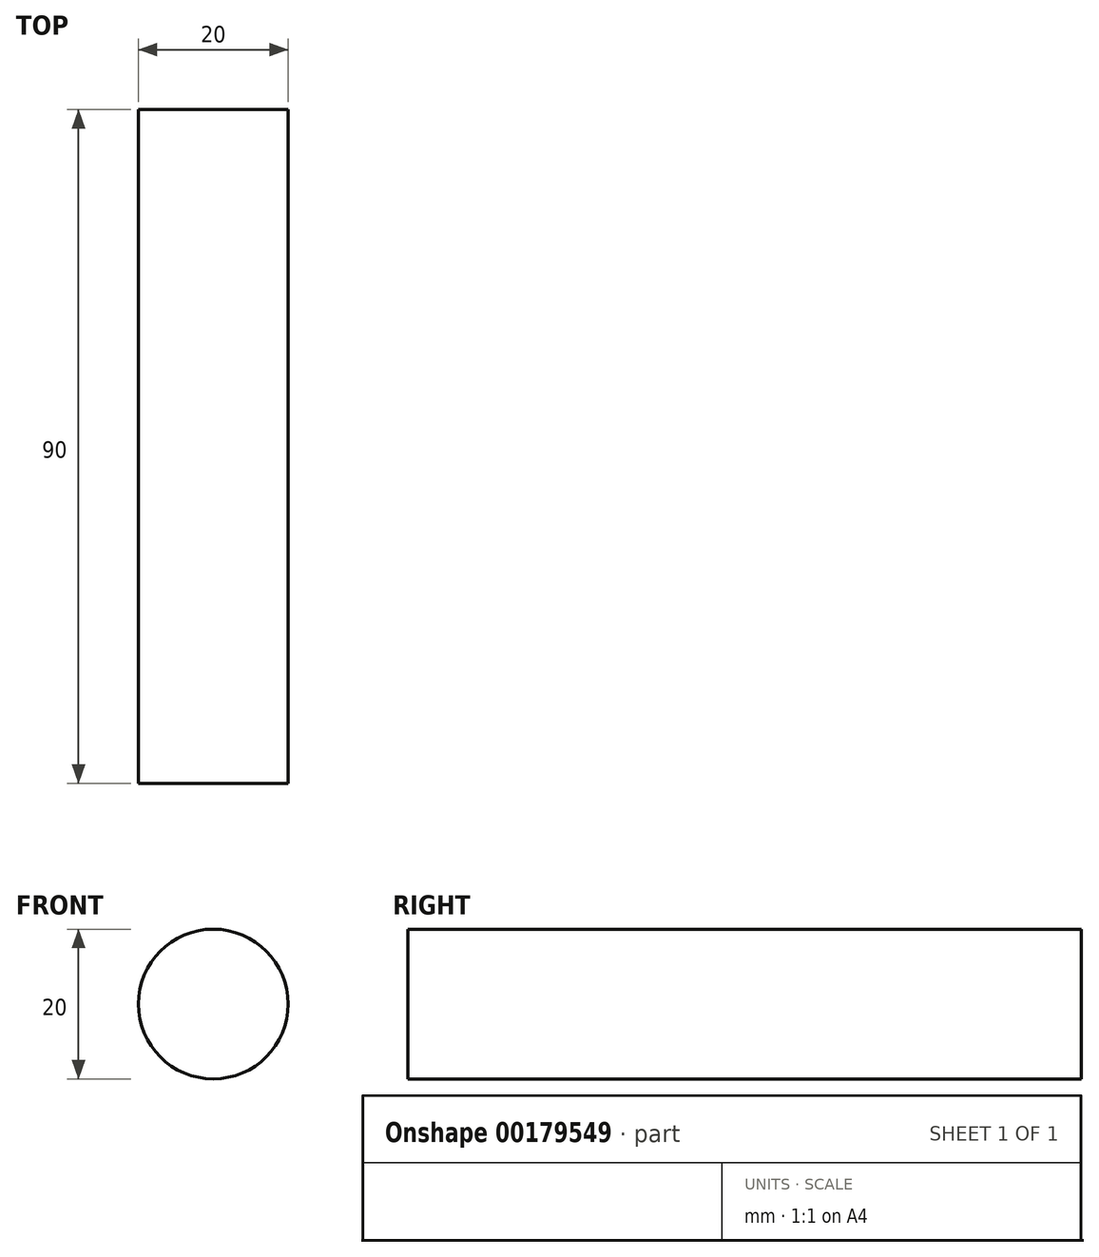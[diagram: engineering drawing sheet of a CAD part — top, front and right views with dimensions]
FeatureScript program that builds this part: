
annotation { "Feature Type Name" : "Feature", "Feature Type Description" : "" }
export const myFeature = defineFeature(function(context is Context, id is Id, definition is map)
    precondition{}
    {
        {
            var Q0;
            Q0=qCreatedBy(makeId("Front.planeOp"),FACE);
            var sketch = newSketch(context, id + "F0", { "sketchPlane" : qUnion([Q0])});
            skCircle(sketch, "E0", {"center": v(0, 0) * mm, "radius": 10 * mm});
            skSolve(sketch);
        }
        {
            var Q0;
            Q0 = qSketchRegion(id + "F0", true);
            extrude(context, id + "F1", {"entities" : qUnion([Q0]), "depth" : 90 * mm});
        }
    });
